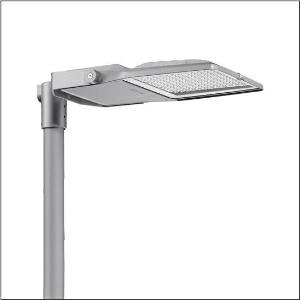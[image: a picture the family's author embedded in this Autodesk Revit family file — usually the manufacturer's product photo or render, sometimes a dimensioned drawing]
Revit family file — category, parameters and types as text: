
# Revit family: floodlight_fl_21_iq_midi___pl64_5xa7782e4e3a_6d1b
name_source: partatom
category: Lighting Fixtures
units: mm (PartAtom-declared; Revit-internal decimal feet)

## family parameters
Cut with Voids When Loaded = No
Host = Face
Light Source = No
Part Type = Normal
Room Calculation Point = No
Round Connector Dimension = Use Diameter
Shared = No

## types (1)
- --- (1 x LED, 27050 lm, 208.1 W, 4000K)
    Apparent Load = 208 VA
    CIE Flux Codes = 28 80 98 100 100
    Color Rendering = 70
    Color Temperature = 4000K
    Default Elevation = 1800 mm
    Description = Floodlight FL 21 iQ midi, floodlight, primary light control with lens, of PMMA, primary optical cover: protective disc, of toughened safety glass, transparent, light distribution: PL64, light emission: direct distribution, installation type: surface-mounted, LED, High Power LED, rated luminous flux: 27.050lm, luminous efficacy: 130lm/W, light colour: 740, colour temperature: 4000K, control gear: ECG iQ, control: optimised constant luminous flux control (CLO 2.0), Desk-Remote (wireless, voltage-free reading and setting of iQ features in the workshop via application-optimized NFC function/RFID function), Smart-Wire, Night-Set, Temp-Guard, Auto-Match, Street-Remote, with terminal, 6-pole, mains connection: 220..240V, AC, 50/60Hz, start of lifetime: 208W, end of service life: 227W, reduction: 90W, luminaire housing, of diecast aluminium, powder-coated, Siteco® metallic grey (DB 702S), corrosivity category C5 mid according to DIN EN ISO 12944, sealing non-destructively replaceable, please order mast flange separately, mast bracket, of steel, galvanised, powder-coated, Siteco® metallic grey (DB 702S), protection rating (complete): IP66, insulation class (complete): insulation class II (safety insulation), certification: CE, protection symbol: D, impact resistance: IK08, permissible operating ambient temperature: -40..+40°C, permissible operating ambient temperature for outdoor applications: -40..+50°C, standard: DIN EN 12944, LABS conformity tested according to VDMA 24364:2018-05, packaging unit: 1 piece

Light Distribution: PL64
    Height = 76 mm
    Lamp = 1 x LED
    Lamp Light Flux = 27050 lm
    Lamp Power = 208.1 W
    Lamp count = 1
    Length = 657 mm
    Luminous efficacy = 130 lm/W
    Manufacturer = Siteco
    ModVariant = No
    Model = 5XA7782E4E3A
    Number of Poles = 1
    OnlyDefault = Yes
    Power Factor = 1
    Product Name = Floodlight FL 21 iQ midi | PL64
    Product group = floodlight | pylon annexe
    ProductGroupID = 6200
    Protection Class = Protection class II
    Protection Degree = IP 66
    RLX_Detail_Level = 1
    RLX_Emergency_Light_Flux = 0 lm
    RLX_Emergency_Type = 0
    RLX_Emergency_Type_DB = No
    RlxData = <blob elided: 153609 chars, md5=366e8384>
    Socket = socket
    Standby Power = 0 W
    System Light Flux = 27050 lm
    System Power = 208 W
    Type Comments = factory setting: luminous flux: 100 % | dim-lin: 254 | 710 mA
    Type Image = l_1007123.jpg
    URL = http://relux.com
    VarID = @adj_055267
    Voltage = 0 V
    Weight = 0.00 kg
    Width = 442 mm

## geometry (parser evidence)
native form markers: Blend x4, Sweep x12
no freeform markers — native parametric forms only
